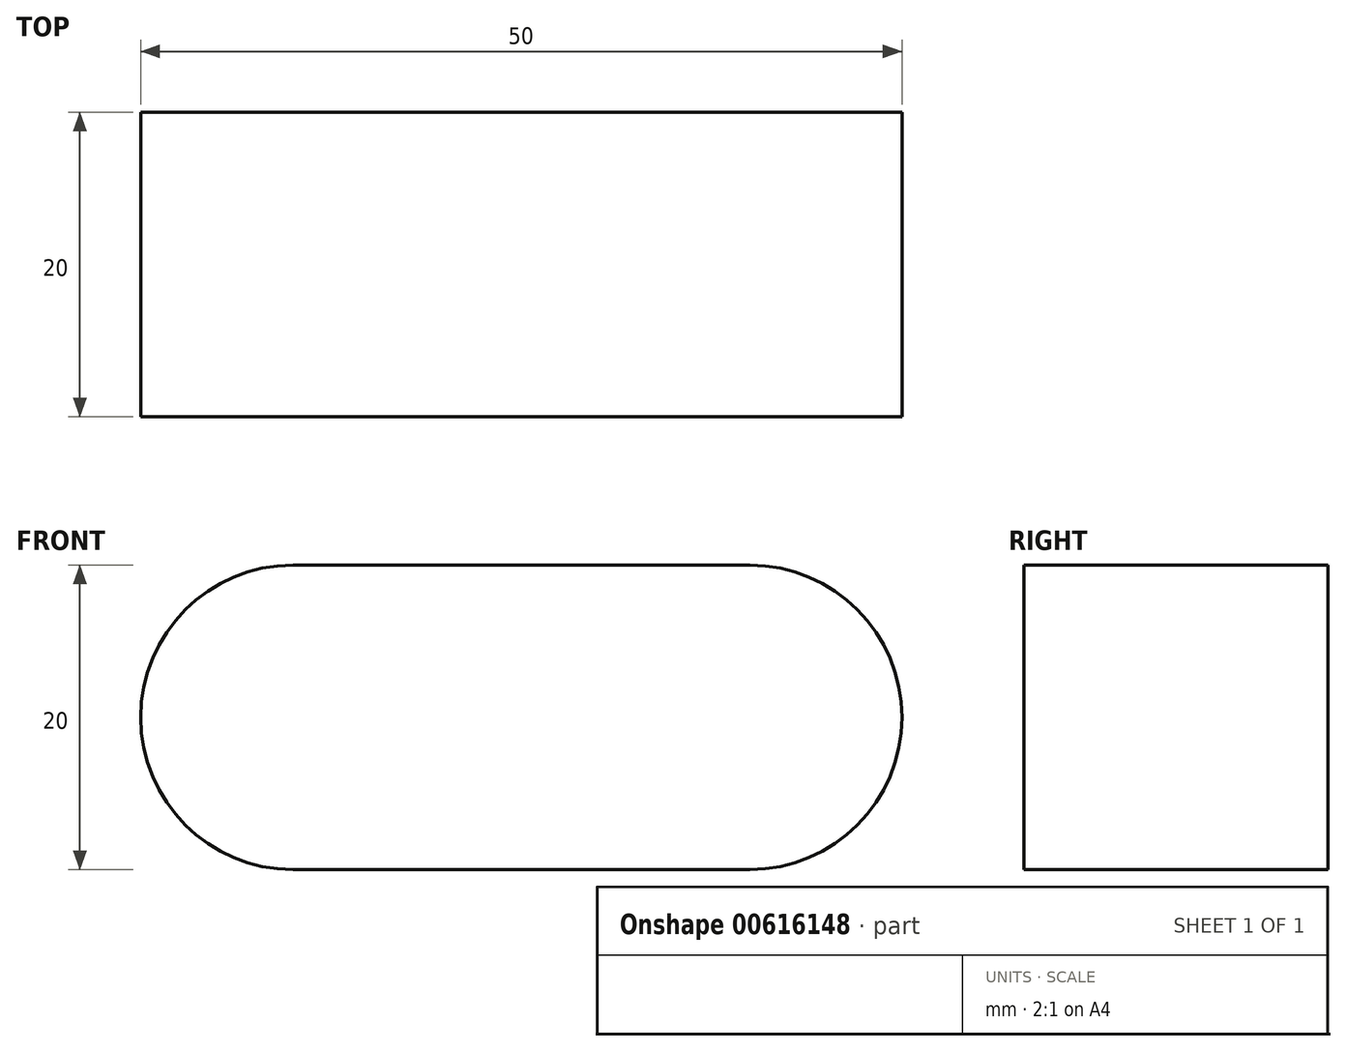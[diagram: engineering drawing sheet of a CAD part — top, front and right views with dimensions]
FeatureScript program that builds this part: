
annotation { "Feature Type Name" : "Feature", "Feature Type Description" : "" }
export const myFeature = defineFeature(function(context is Context, id is Id, definition is map)
    precondition{}
    {
        {
            var Q0;
            Q0=qCreatedBy(makeId("Top.planeOp"),FACE);
            var sketch = newSketch(context, id + "F0", { "sketchPlane" : qUnion([Q0])});
            skLineSegment(sketch, "E0.bottom", {"start": v(-50, 20) * mm, "end": v(0, 20) * mm});
            skLineSegment(sketch, "E0.top", {"start": v(-50, 0) * mm, "end": v(0, 0) * mm});
            skLineSegment(sketch, "E0.left", {"start": v(-50, 20) * mm, "end": v(-50, 0) * mm});
            skLineSegment(sketch, "E0.right", {"start": v(0, 20) * mm, "end": v(0, 0) * mm});
            skSolve(sketch);
        }
        {
            var Q0;
            Q0 = qSketchRegion(id + "F0", true);
            extrude(context, id + "F1", {"entities" : qUnion([Q0]), "depth" : 20 * mm, "offsetDistance" : 25 * mm});
        }
        {
            var Q0;
            Q0=makeQuery(id+"F1.opExtrude","CAP_EDGE",EDGE,{"disambiguationData":[OSD([sQuery(id+"F0.wireOp",EDGE,"E0.left")])],"isStart":false});
            var Q1;
            Q1=makeQuery(id+"F1.opExtrude","CAP_EDGE",EDGE,{"disambiguationData":[OSD([sQuery(id+"F0.wireOp",EDGE,"E0.right")])],"isStart":false});
            var Q2;
            Q2=makeQuery(id+"F1.opExtrude","CAP_EDGE",EDGE,{"disambiguationData":[OSD([sQuery(id+"F0.wireOp",EDGE,"E0.right")])],"isStart":true});
            var Q3;
            Q3=makeQuery(id+"F1.opExtrude","CAP_EDGE",EDGE,{"disambiguationData":[OSD([sQuery(id+"F0.wireOp",EDGE,"E0.left")])],"isStart":true});
            fillet(context, id + "F2", {"entities" : qUnion([Q0, Q1, Q2, Q3]), "radius" : 10 * mm, "tangentPropagation" : true, "allowEdgeOverflow" : false});
        }
    });
